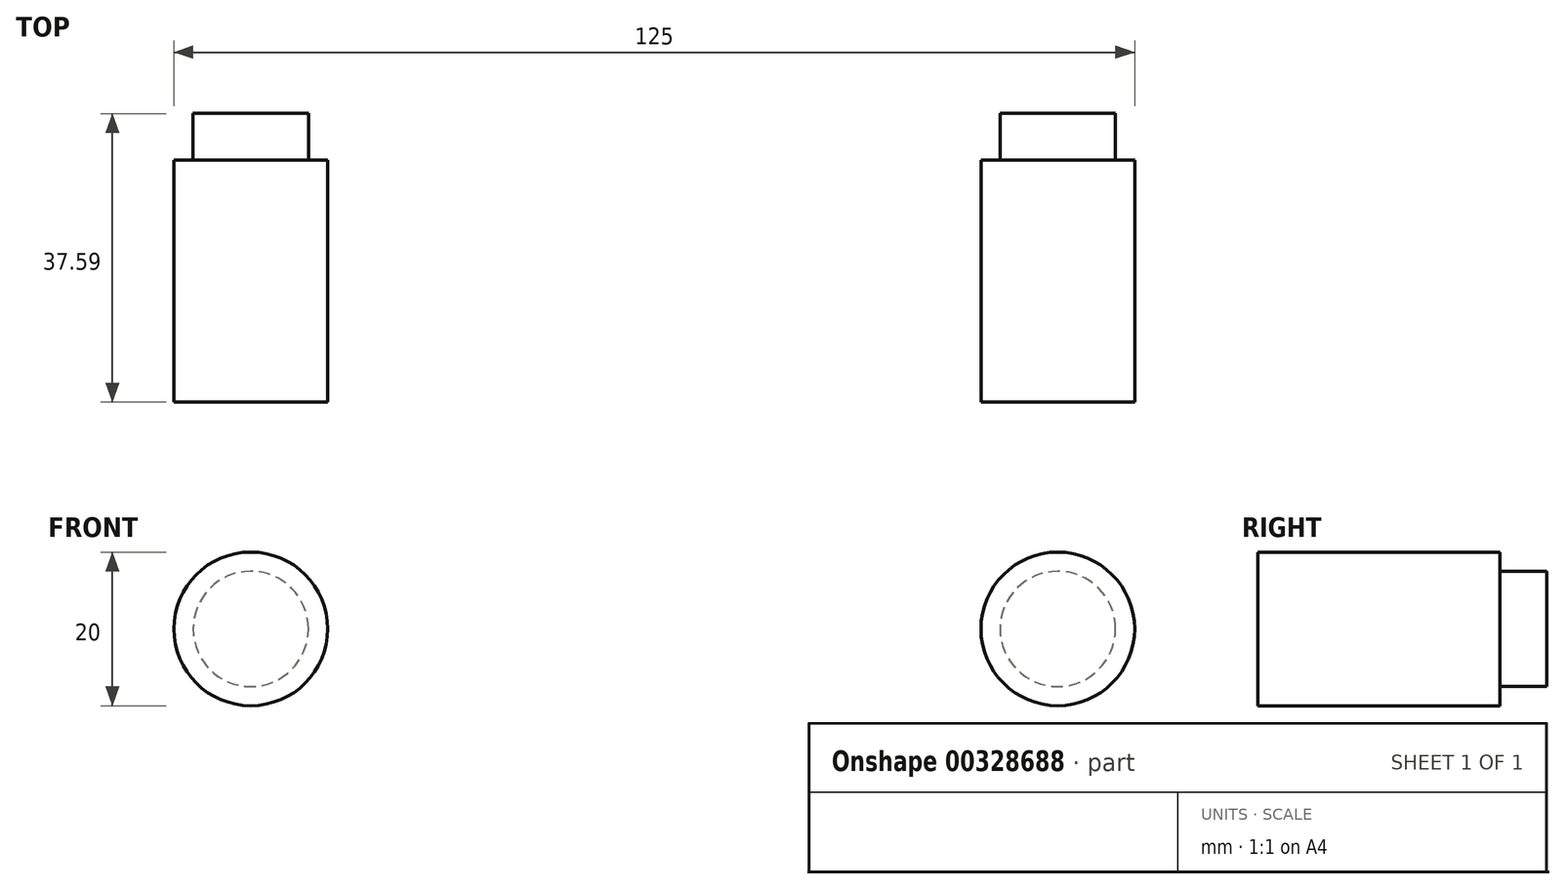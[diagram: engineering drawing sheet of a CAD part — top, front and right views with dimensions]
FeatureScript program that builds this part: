
annotation { "Feature Type Name" : "Feature", "Feature Type Description" : "" }
export const myFeature = defineFeature(function(context is Context, id is Id, definition is map)
    precondition{}
    {
        {
            var Q0;
            Q0=qCreatedBy(makeId("Front.planeOp"),FACE);
            var sketch = newSketch(context, id + "F0", { "sketchPlane" : qUnion([Q0])});
            skCircle(sketch, "E0", {"center": v(-41.73, 0) * mm, "radius": 10 * mm});
            skCircle(sketch, "E1", {"center": v(63.27, 0) * mm, "radius": 10 * mm});
            skSolve(sketch);
        }
        {
            var Q0;
            Q0 = qSketchRegion(id + "F0", true);
            extrude(context, id + "F1", {"entities" : qUnion([Q0]), "oppositeDirection" : true, "depth" : 31.5 * mm});
        }
        {
            var Q0;
            Q0=makeQuery(id+"F1.opExtrude","CAP_FACE",FACE,{"disambiguationData":[OSD([sQuery(id+"F0.wireOp",EDGE,"E0")])],"isStart":false});
            var sketch = newSketch(context, id + "F2", { "sketchPlane" : qUnion([Q0])});
            skCircle(sketch, "E2", {"center": v(41.73, 0) * mm, "radius": 7.5 * mm});
            skCircle(sketch, "E3", {"center": v(-63.27, 0) * mm, "radius": 7.5 * mm});
            skSolve(sketch);
        }
        {
            var Q0;
            Q0 = qSketchRegion(id + "F2", true);
            extrude(context, id + "F3", {"entities" : qUnion([Q0]), "depth" : 6.1 * mm});
        }
    });
